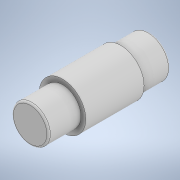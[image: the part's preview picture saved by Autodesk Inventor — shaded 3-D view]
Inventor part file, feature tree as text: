
AUTODESK INVENTOR PART (.ipt)
format: ipt  version: 2020.3 (Build 243373000, 373)  size: 125,952 bytes
history: native  units: mm
features: extrude x3, sketch x3, fillet x1
ambient origin geometry x8: Origin, YZ Plane, XZ Plane, XY Plane, X Axis, Y Axis, Z Axis, Center Point
bodies: Solid1 (feature_tree)
feature tree (7):
  extrude  "Extrusion1"  Depth=5.0mm TaperAngle=0.0deg
  extrude  "Extrusion2"  Depth=10.0mm TaperAngle=0.0deg
  extrude  "Extrusion3"  Depth=5.556mm TaperAngle=0.0deg
  fillet  "Fillet1"  Radius=0.3mm
  sketch  "Sketch1"  dims[d0=7.0mm d1=5.0mm d2=0.0mm]
  sketch  "Sketch2"  dims[d3=8.0mm d4=10.0mm d5=0.0mm]
  sketch  "Sketch3"  dims[d6=6.35mm d7=5.556mm d8=0.0mm d9=0.3mm]
